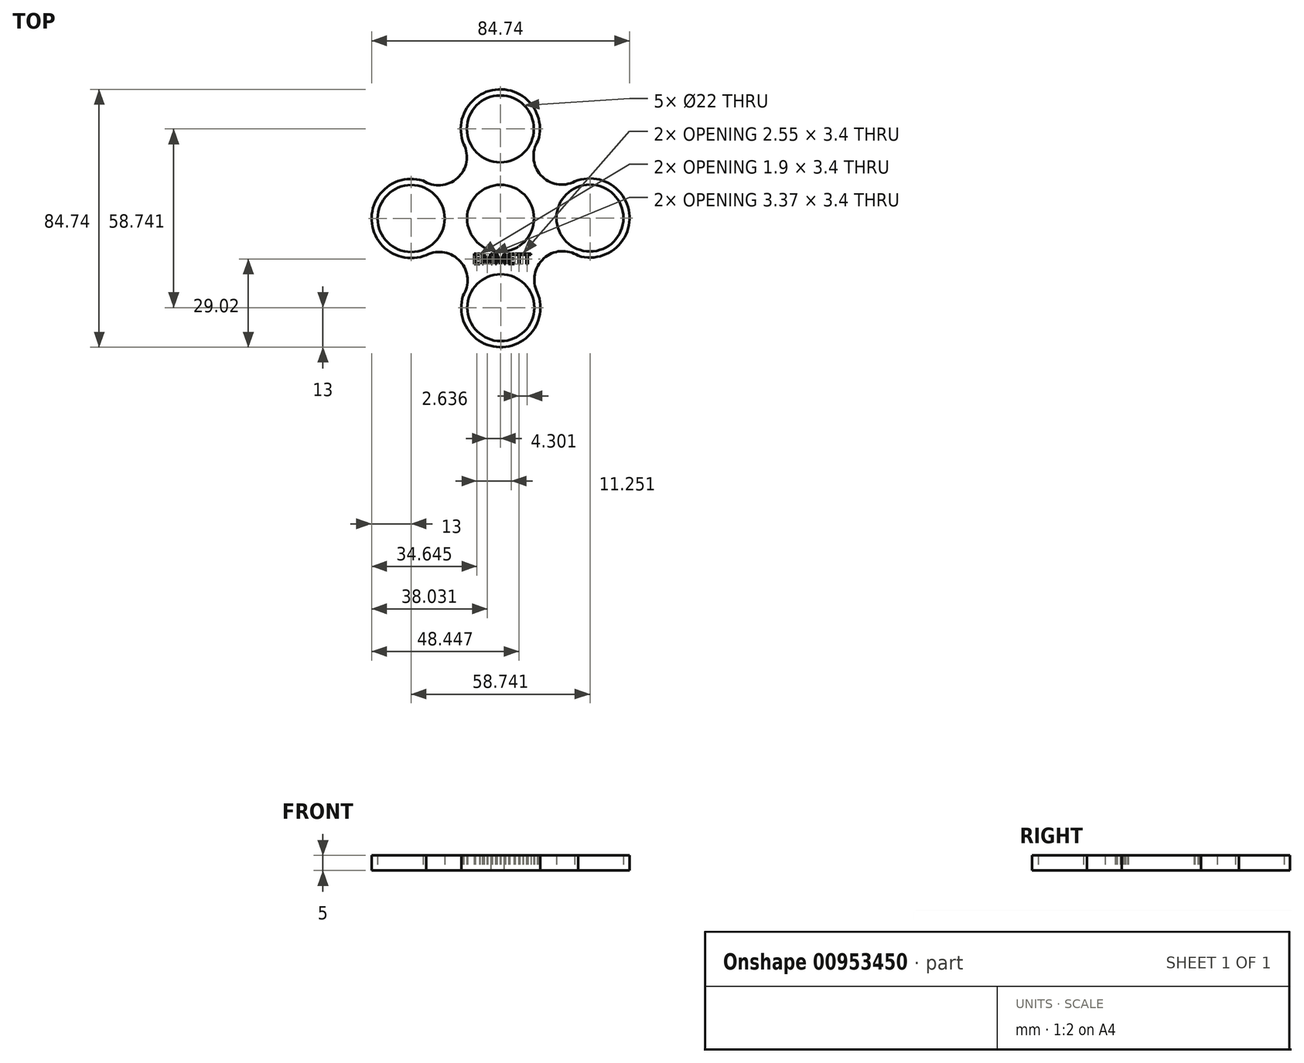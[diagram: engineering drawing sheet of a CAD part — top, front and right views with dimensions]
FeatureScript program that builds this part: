
annotation { "Feature Type Name" : "Feature", "Feature Type Description" : "" }
export const myFeature = defineFeature(function(context is Context, id is Id, definition is map)
    precondition{}
    {
        {
            var Q0;
            Q0=qCreatedBy(makeId("Top.planeOp"),FACE);
            var sketch = newSketch(context, id + "F0", { "sketchPlane" : qUnion([Q0])});
            skCircle(sketch, "E0", {"center": v(0, 0) * mm, "radius": 11 * mm});
            skCircle(sketch, "E1", {"center": v(-0.08, 29.37) * mm, "radius": 11 * mm});
            skCircle(sketch, "E2.1.0", {"center": v(-29.37, -0.08) * mm, "radius": 11 * mm});
            skCircle(sketch, "E2.2.0", {"center": v(0.08, -29.37) * mm, "radius": 11 * mm});
            skCircle(sketch, "E2.3.0", {"center": v(29.37, 0.08) * mm, "radius": 11 * mm});
            skCircle(sketch, "E3", {"center": v(-0.08, 29.37) * mm, "radius": 13 * mm});
            skCircle(sketch, "E4.1.0", {"center": v(-29.37, -0.08) * mm, "radius": 13 * mm});
            skCircle(sketch, "E4.2.0", {"center": v(0.08, -29.37) * mm, "radius": 13 * mm});
            skCircle(sketch, "E5.1.3.0", {"center": v(29.37, 0.08) * mm, "radius": 13 * mm});
            skArc(sketch, "E6", {"start": v(25.5, -12.33) * mm, "mid": v(14.17, -13.2) * mm, "end": v(12.08, -24.37) * mm});
            skArc(sketch, "E7.1.0", {"start": v(12.33, 25.5) * mm, "mid": v(13.2, 14.17) * mm, "end": v(24.37, 12.08) * mm});
            skArc(sketch, "E7.2.0", {"start": v(-25.5, 12.33) * mm, "mid": v(-14.17, 13.2) * mm, "end": v(-12.08, 24.37) * mm});
            skArc(sketch, "E7.3.0", {"start": v(-12.33, -25.5) * mm, "mid": v(-13.2, -14.17) * mm, "end": v(-24.37, -12.08) * mm});
            skText(sketch, "E8", { "text": "EMMETT", "fontName": "OpenSans-Regular.ttf"});
            const initialGuessF0  = {"E8": [-0.00914, -0.01505, 1, 0, 0.00343]};
            skSetInitialGuess(sketch, initialGuessF0);
            skSolve(sketch);
        }
        {
            var Q0;
            Q0=makeQuery(id+"F0.imprint","IMPRINT",FACE,{"disambiguationData":[TD([[makeQuery(id+"F0.imprint","IMPRINT",EDGE,{"derivedFrom":sQuery(id+"F0.wireOp",EDGE,"E2.3.0")}),-1.0]])]});
            var Q1;
            Q1=makeQuery(id+"F0.imprint","IMPRINT",FACE,{"disambiguationData":[TD([[makeQuery(id+"F0.imprint","IMPRINT",EDGE,{"derivedFrom":sQuery(id+"F0.wireOp",EDGE,"E2.2.0")}),-1.0]])]});
            var Q2;
            Q2=makeQuery(id+"F0.imprint","IMPRINT",FACE,{"disambiguationData":[TD([[makeQuery(id+"F0.imprint","IMPRINT",EDGE,{"derivedFrom":sQuery(id+"F0.wireOp",EDGE,"E2.1.0")}),-1.0]])]});
            var Q3;
            Q3=makeQuery(id+"F0.imprint","IMPRINT",FACE,{"disambiguationData":[TD([[makeQuery(id+"F0.imprint","IMPRINT",EDGE,{"derivedFrom":sQuery(id+"F0.wireOp",EDGE,"E1")}),-1.0]])]});
            var Q4;
            Q4=makeQuery(id+"F0.imprint","IMPRINT",FACE,{"disambiguationData":[TD([[makeQuery(id+"F0.imprint","IMPRINT",EDGE,{"derivedFrom":sQuery(id+"F0.wireOp",EDGE,"E0")}),-1.0]])]});
            extrude(context, id + "F1", {"entities" : qUnion([Q0, Q1, Q2, Q3, Q4]), "depth" : 5 * mm, "offsetDistance" : 25 * mm});
        }
    });
